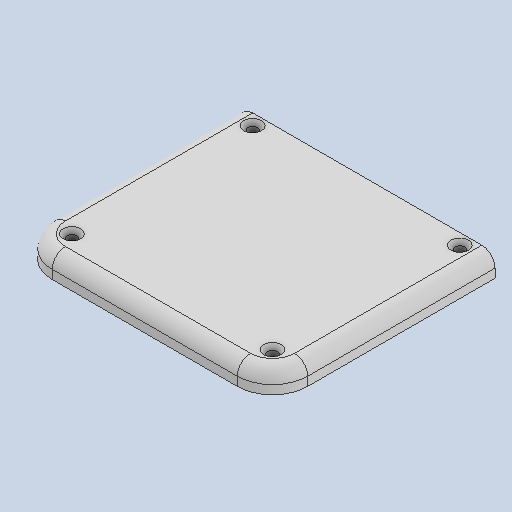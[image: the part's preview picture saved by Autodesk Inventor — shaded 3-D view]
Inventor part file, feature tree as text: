
AUTODESK INVENTOR PART (.ipt)
format: ipt  version: 2022.3 (Build 263350000, 350)  size: 186,368 bytes
history: native  units: mm
features: sketch x3, extrude x2, fillet x2, hole x1, thicken_offset x1, projected_geometry x1
ambient origin geometry x8: Origin, YZ Plane, XZ Plane, XY Plane, X Axis, Y Axis, Z Axis, Center Point
bodies: Solid1 (feature_tree)
feature tree (10):
  extrude  "Extrusion1"  Depth=47.5mm
  fillet  "Fillet1"  Radius=3.0mm
  extrude  "Extrusion2"  Depth=3.0mm
  hole  "Hole1"  [1 undecoded]
  fillet  "Fillet2"  Radius=3.0mm
  thicken_offset  "Thicken1"
  sketch  "Sketch1"  dims[d0=52.0mm d1=47.5mm d2=3.0mm d3=0.0mm]
  sketch  "Sketch2"  dims[d4=5.0mm d5=3.0mm]
  projected_geometry  "Projected Loop1"
  sketch  "Sketch3"  dims[d6=5.0mm d7=0.0mm d8=3.0mm d9=3.0mm d10=5.0mm d11=5.0mm d12=3.0mm d13=3.0mm d14=5.0mm d15=5.0mm d16=37.5mm d17=5.0mm d18=5.0mm d19=5.0mm d20=135.0deg d21=5.0mm d22=2.2mm d23=6.0mm d24=4.0mm d25=2.0mm d26=90.0deg d27=2.2mm d28=0.0mm d29=3.0mm d30=3.0mm d31=3.0mm]
note: 1 required parameter value undecoded (feature->parameter linkage not recoverable at this tier; creation-order binding heuristic only, values carry confidence <= 0.55)
